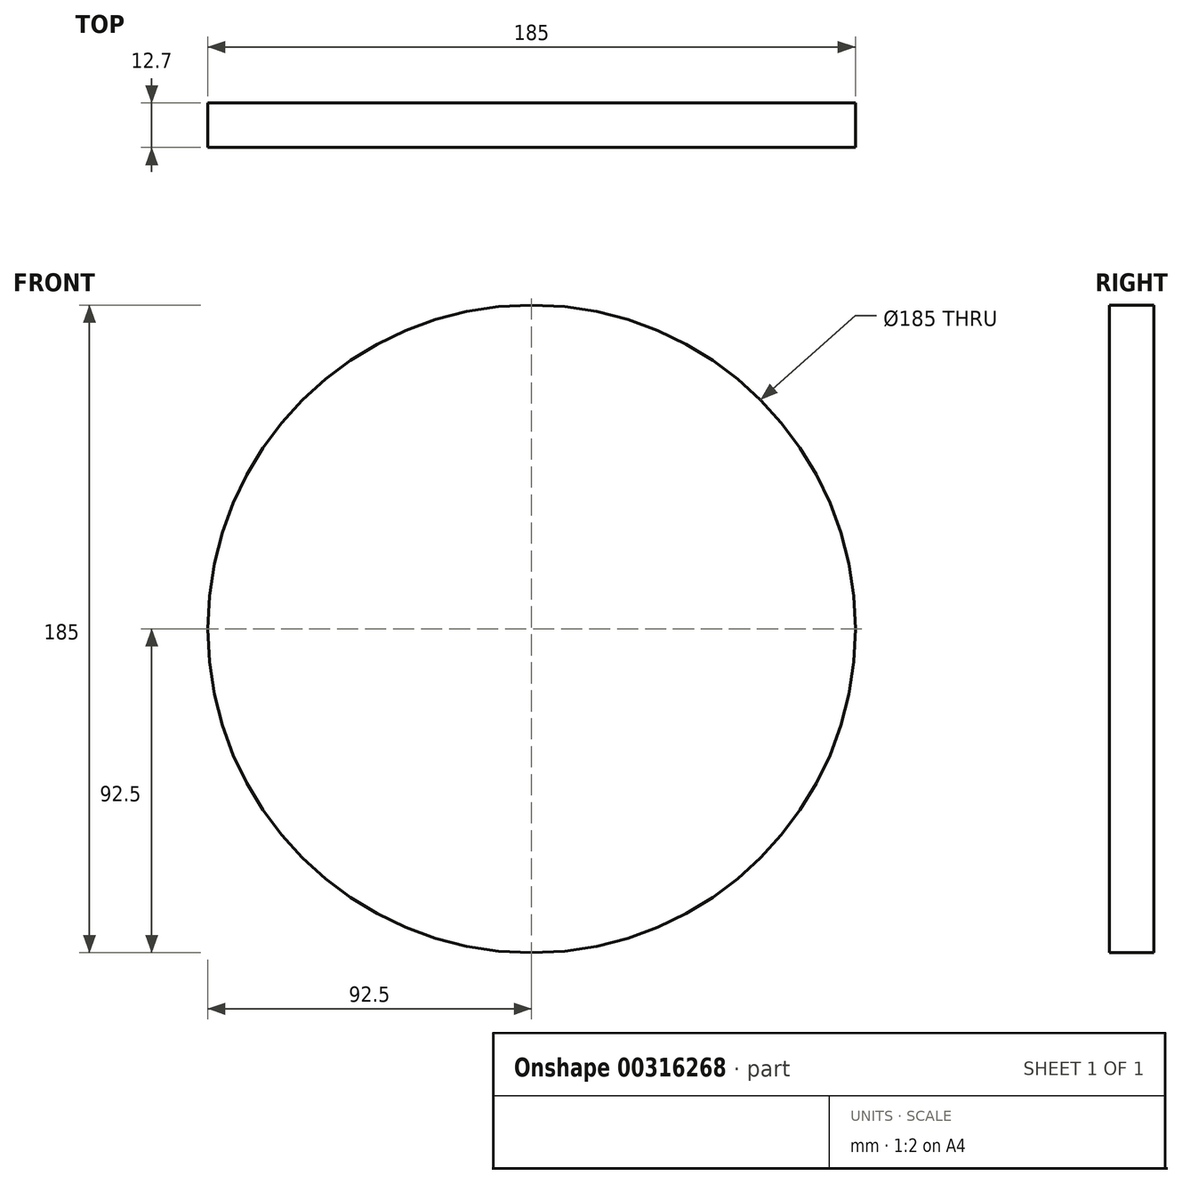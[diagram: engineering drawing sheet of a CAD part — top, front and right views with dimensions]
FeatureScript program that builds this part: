
annotation { "Feature Type Name" : "Feature", "Feature Type Description" : "" }
export const myFeature = defineFeature(function(context is Context, id is Id, definition is map)
    precondition{}
    {
        {
            var Q0;
            Q0=qCreatedBy(makeId("Front.planeOp"),FACE);
            var sketch = newSketch(context, id + "F0", { "sketchPlane" : qUnion([Q0])});
            skCircle(sketch, "E0", {"center": v(0, 0) * mm, "radius": 92.5 * mm});
            skSolve(sketch);
        }
        {
            var Q0;
            Q0=sQuery(id+"Fi7Oh2Qj9PqHzAU_0.wireOp",EDGE,"sNH7Jsex-Zfxg-SoKn-CUdg-KH3TS65b55RC");
            var Q1;
            Q1=sQuery(id+"F0.wireOp",EDGE,"E0");
            extrude(context, id + "F1", {"bodyType" : ToolBodyType.SURFACE, "surfaceEntities" : qUnion([Q0, Q1]), "oppositeDirection" : true, "depth" : 12.7 * mm});
        }
    });
